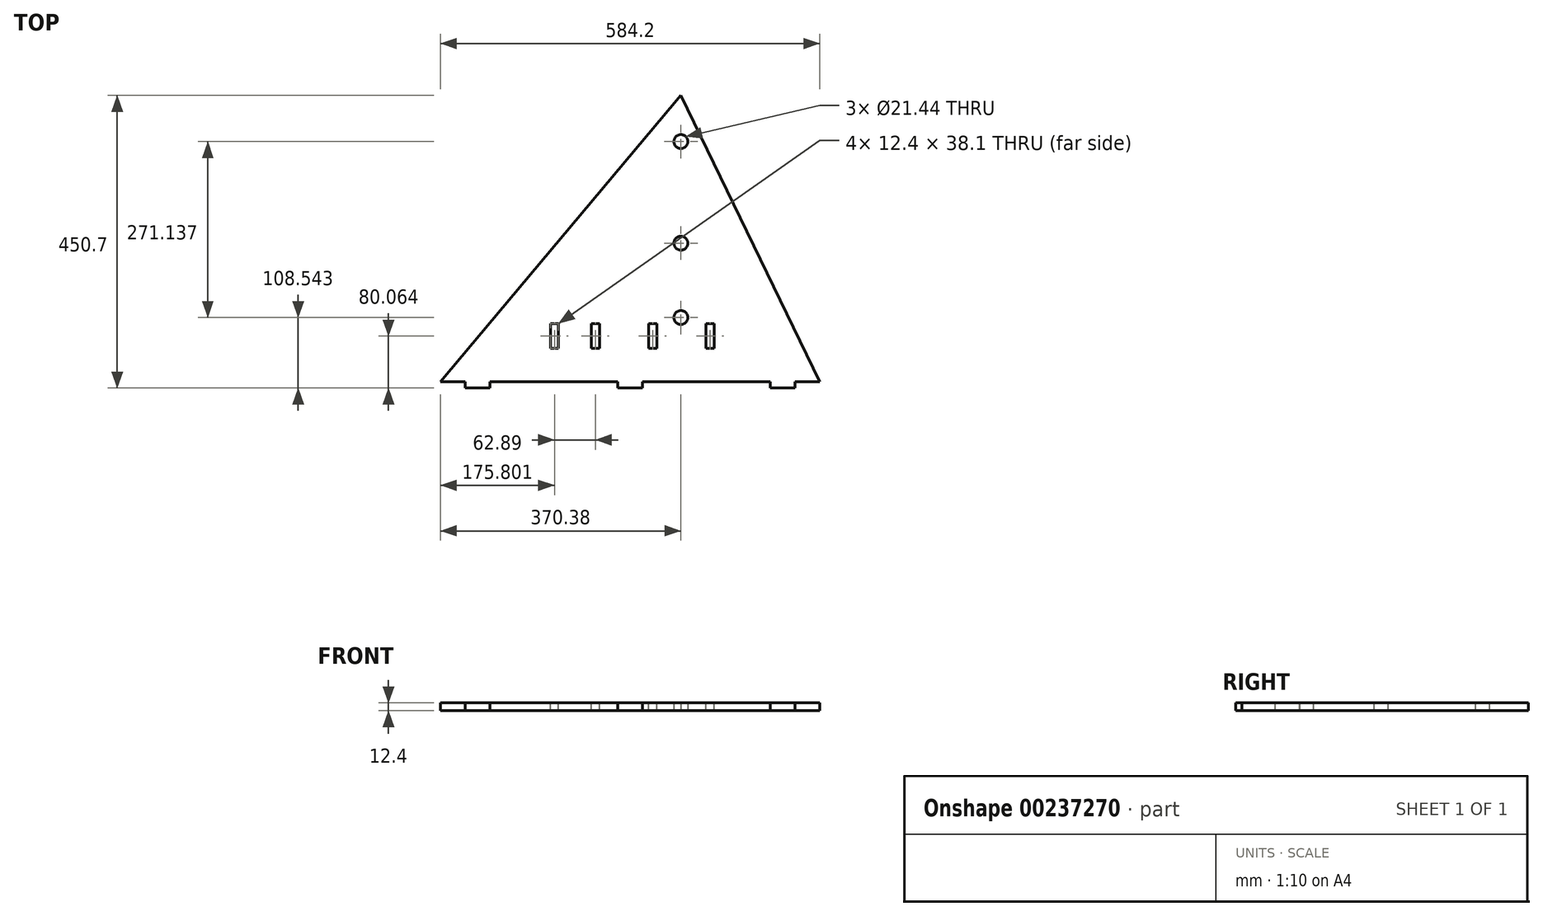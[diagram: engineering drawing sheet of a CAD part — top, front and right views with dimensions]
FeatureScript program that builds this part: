
annotation { "Feature Type Name" : "Feature", "Feature Type Description" : "" }
export const myFeature = defineFeature(function(context is Context, id is Id, definition is map)
    precondition{}
    {
        {
            var Q0;
            Q0=qCreatedBy(makeId("Top.planeOp"),FACE);
            var sketch = newSketch(context, id + "F0", { "sketchPlane" : qUnion([Q0])});
            skLineSegment(sketch, "E0", {"start": v(0, 0) * mm, "end": v(584.2, 0) * mm});
            skLineSegment(sketch, "E1", {"start": v(0, 0) * mm, "end": v(370.38, 441.4) * mm});
            skLineSegment(sketch, "E2", {"start": v(370.38, 441.4) * mm, "end": v(584.2, 0) * mm});
            skLineSegment(sketch, "E3", {"start": v(370.38, 441.4) * mm, "end": v(370.38, 0) * mm});
            skCircle(sketch, "E4", {"center": v(370.38, 99.24) * mm, "radius": 10.72 * mm});
            skCircle(sketch, "E5", {"center": v(370.38, 213.84) * mm, "radius": 10.72 * mm});
            skCircle(sketch, "E6", {"center": v(370.38, 370.38) * mm, "radius": 10.72 * mm});
            skSolve(sketch);
        }
        {
            var Q0;
            {var subQ0=sQuery(id+"F0.wireOp",EDGE,"E1");Q0=makeQuery(id+"F0.imprint","IMPRINT",FACE,{"disambiguationData":[TD([[makeQuery(id+"F0.imprint","IMPRINT",EDGE,{"derivedFrom":subQ0}),-1.0]])]});}
            var Q1;
            {var subQ0=sQuery(id+"F0.wireOp",EDGE,"E2");Q1=makeQuery(id+"F0.imprint","IMPRINT",FACE,{"disambiguationData":[TD([[makeQuery(id+"F0.imprint","IMPRINT",EDGE,{"derivedFrom":subQ0}),-1.0]])]});}
            extrude(context, id + "F1", {"entities" : qUnion([Q0, Q1]), "depth" : 12.4 * mm});
        }
        {
            var Q0;
            Q0=makeQuery(id+"F1.opExtrude","SWEPT_FACE",FACE,{"disambiguationData":[OSD([sQuery(id+"F0.wireOp",EDGE,"E0")])]});
            var sketch = newSketch(context, id + "F2", { "sketchPlane" : qUnion([Q0])});
            skLineSegment(sketch, "E7.bottom", {"start": v(38.1, 0) * mm, "end": v(76.2, 0) * mm});
            skLineSegment(sketch, "E7.top", {"start": v(38.1, 12.4) * mm, "end": v(76.2, 12.4) * mm});
            skLineSegment(sketch, "E7.left", {"start": v(38.1, 0) * mm, "end": v(38.1, 12.4) * mm});
            skLineSegment(sketch, "E7.right", {"start": v(76.2, 0) * mm, "end": v(76.2, 12.4) * mm});
            skLineSegment(sketch, "E8.bottom", {"start": v(273.05, 0) * mm, "end": v(311.15, 0) * mm});
            skLineSegment(sketch, "E8.top", {"start": v(273.05, 12.4) * mm, "end": v(311.15, 12.4) * mm});
            skLineSegment(sketch, "E8.left", {"start": v(273.05, 0) * mm, "end": v(273.05, 12.4) * mm});
            skLineSegment(sketch, "E8.right", {"start": v(311.15, 0) * mm, "end": v(311.15, 12.4) * mm});
            skLineSegment(sketch, "E9.bottom", {"start": v(546.1, 12.4) * mm, "end": v(508, 12.4) * mm});
            skLineSegment(sketch, "E9.top", {"start": v(546.1, 0) * mm, "end": v(508, 0) * mm});
            skLineSegment(sketch, "E9.left", {"start": v(546.1, 12.4) * mm, "end": v(546.1, 0) * mm});
            skLineSegment(sketch, "E9.right", {"start": v(508, 12.4) * mm, "end": v(508, 0) * mm});
            skSolve(sketch);
        }
        {
            var Q0;
            Q0=makeQuery(id+"F2.imprint","IMPRINT",FACE,{"disambiguationData":[TD([[makeQuery(id+"F2.imprint","IMPRINT",EDGE,{"derivedFrom":sQuery(id+"F2.wireOp",EDGE,"E7.bottom")}),1.0]])]});
            var Q1;
            Q1=makeQuery(id+"F2.imprint","IMPRINT",FACE,{"disambiguationData":[TD([[makeQuery(id+"F2.imprint","IMPRINT",EDGE,{"derivedFrom":sQuery(id+"F2.wireOp",EDGE,"E8.bottom")}),1.0]])]});
            var Q2;
            Q2=makeQuery(id+"F2.imprint","IMPRINT",FACE,{"disambiguationData":[TD([[makeQuery(id+"F2.imprint","IMPRINT",EDGE,{"derivedFrom":sQuery(id+"F2.wireOp",EDGE,"E9.bottom")}),-1.0]])]});
            extrude(context, id + "F3", {"entities" : qUnion([Q0, Q1, Q2]), "operationType" : NewBodyOperationType.ADD, "depth" : 9.3 * mm});
        }
        {
            var Q0;
            Q0=makeQuery(id+"F3.boolean.opBoolean","MERGE",FACE,{"derivedFrom":[makeQuery(id+"F1.opExtrude","CAP_FACE",FACE,{"disambiguationData":[OSD([sQuery(id+"F0.wireOp",EDGE,"E0"),sQuery(id+"F0.wireOp",EDGE,"E1"),sQuery(id+"F0.wireOp",EDGE,"E2"),sQuery(id+"F0.wireOp",EDGE,"hbV72auo-273c-H3mX-hN14-NdLNeiQO2f8u"),sQuery(id+"F0.wireOp",EDGE,"yJkv0m9N-xar6-jenL-caYz-NCVx4oEyzwZq"),sQuery(id+"F0.wireOp",EDGE,"0IbjTIdv-al9A-gIdp-c788-NeGzfYGJylQS"),sQuery(id+"F0.wireOp",EDGE,"PPQqT81c-MBrL-Zwf6-FBoo-YlBdeRjJLvez"),sQuery(id+"F0.wireOp",EDGE,"1zVKnzYX-4IMU-bpsW-vgjR-UfY4y7IhUxRJ"),sQuery(id+"F0.wireOp",EDGE,"5PhSZh7U-XTF8-9HuU-3B06-5hTz75dbE28A"),sQuery(id+"F0.wireOp",EDGE,"QVwwZdeT-OtHh-xgnp-WqoG-H6M2aq466ZE5"),sQuery(id+"F0.wireOp",EDGE,"ByblHu9g-uYND-DHe2-2H8c-uT3Bsr3WFWiR"),sQuery(id+"F0.wireOp",EDGE,"q02sBKiU-ZI61-Ygqg-VMs2-e9jpUoOFu8LE"),sQuery(id+"F0.wireOp",EDGE,"yCSYR6cb-g6EO-dpne-vkbb-vtuTMJx8oQwn"),sQuery(id+"F0.wireOp",EDGE,"idvjweJo-wAV1-CoL9-3O4M-DzAfA2Q9TY8j"),sQuery(id+"F0.wireOp",EDGE,"c9bJ2uXe-l4rV-DpG6-cNZs-KjiGAo79kyFT"),sQuery(id+"F0.wireOp",EDGE,"7UX84spq-HRxE-01sJ-ZdLk-nk1ZSfVjff84"),sQuery(id+"F0.wireOp",EDGE,"KV4dBIfH-gvWu-Nq0R-Qmzo-mCH37MA8YzNq"),sQuery(id+"F0.wireOp",EDGE,"51JhfH0C-1wzP-8lwW-ZeS3-U5hvUvuMjHKp")])],"isStart":false}),makeQuery(id+"F3.opExtrude","SWEPT_FACE",FACE,{"disambiguationData":[OSD([sQuery(id+"F2.wireOp",EDGE,"E7.top")])]}),makeQuery(id+"F3.opExtrude","SWEPT_FACE",FACE,{"disambiguationData":[OSD([sQuery(id+"F2.wireOp",EDGE,"E8.top")])]}),makeQuery(id+"F3.opExtrude","SWEPT_FACE",FACE,{"disambiguationData":[OSD([sQuery(id+"F2.wireOp",EDGE,"E9.bottom")])]})]});
            var sketch = newSketch(context, id + "F4", { "sketchPlane" : qUnion([Q0])});
            skLineSegment(sketch, "E10.bottom", {"start": v(232.5, 89.81) * mm, "end": v(244.89, 89.81) * mm});
            skLineSegment(sketch, "E10.top", {"start": v(232.5, 51.71) * mm, "end": v(244.89, 51.71) * mm});
            skLineSegment(sketch, "E10.left", {"start": v(232.5, 89.81) * mm, "end": v(232.5, 51.71) * mm});
            skLineSegment(sketch, "E10.right", {"start": v(244.89, 89.81) * mm, "end": v(244.89, 51.71) * mm});
            skLineSegment(sketch, "E11.bottom", {"start": v(320.78, 89.81) * mm, "end": v(333.18, 89.81) * mm});
            skLineSegment(sketch, "E11.top", {"start": v(320.78, 51.71) * mm, "end": v(333.18, 51.71) * mm});
            skLineSegment(sketch, "E11.left", {"start": v(320.78, 89.81) * mm, "end": v(320.78, 51.71) * mm});
            skLineSegment(sketch, "E11.right", {"start": v(333.18, 89.81) * mm, "end": v(333.18, 51.71) * mm});
            skLineSegment(sketch, "E12.bottom", {"start": v(409.07, 89.81) * mm, "end": v(421.47, 89.81) * mm});
            skLineSegment(sketch, "E12.top", {"start": v(409.07, 51.71) * mm, "end": v(421.47, 51.71) * mm});
            skLineSegment(sketch, "E12.left", {"start": v(409.07, 89.81) * mm, "end": v(409.07, 51.71) * mm});
            skLineSegment(sketch, "E12.right", {"start": v(421.47, 89.81) * mm, "end": v(421.47, 51.71) * mm});
            skLineSegment(sketch, "E13.bottom", {"start": v(182, 89.81) * mm, "end": v(169.6, 89.81) * mm});
            skLineSegment(sketch, "E13.top", {"start": v(182, 51.71) * mm, "end": v(169.6, 51.71) * mm});
            skLineSegment(sketch, "E13.left", {"start": v(182, 89.81) * mm, "end": v(182, 51.71) * mm});
            skLineSegment(sketch, "E13.right", {"start": v(169.6, 89.81) * mm, "end": v(169.6, 51.71) * mm});
            skLineSegment(sketch, "E14", {"start": v(370.38, 441.4) * mm, "end": v(370.38, 0) * mm, "construction": true});
            skSolve(sketch);
        }
        {
            var Q0;
            Q0 = qSketchRegion(id + "F4", true);
            extrude(context, id + "F5", {"entities" : qUnion([Q0]), "operationType" : NewBodyOperationType.REMOVE, "endBound" : BoundingType.UP_TO_NEXT, "oppositeDirection" : true, "depth" : 12.4 * mm});
        }
    });
